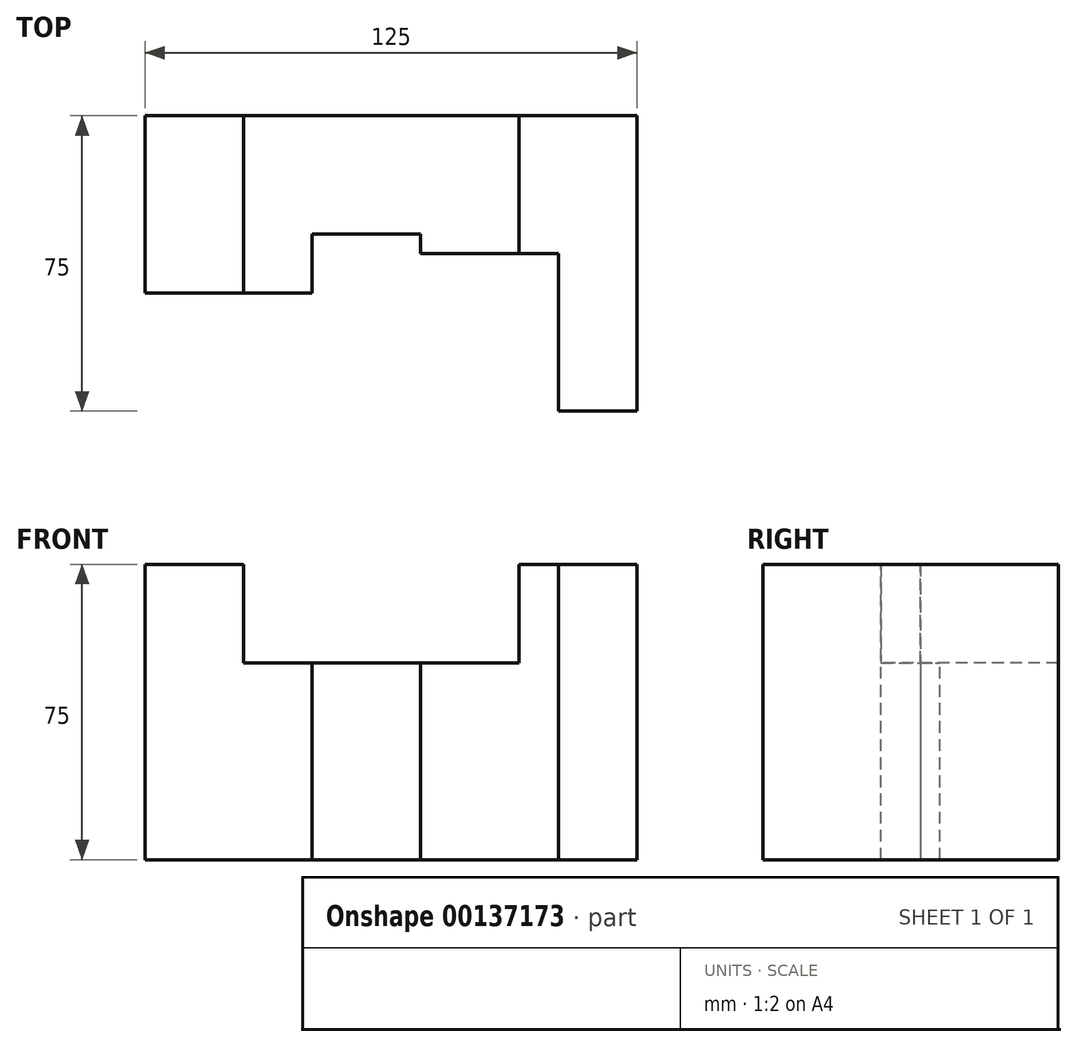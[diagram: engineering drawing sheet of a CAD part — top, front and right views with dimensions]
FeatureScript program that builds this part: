
annotation { "Feature Type Name" : "Feature", "Feature Type Description" : "" }
export const myFeature = defineFeature(function(context is Context, id is Id, definition is map)
    precondition{}
    {
        {
            var Q0;
            Q0=qCreatedBy(makeId("Front.planeOp"),FACE);
            var sketch = newSketch(context, id + "F0", { "sketchPlane" : qUnion([Q0])});
            skLineSegment(sketch, "E0.bottom", {"start": v(-62.95, 0) * mm, "end": v(62.05, 0) * mm});
            skLineSegment(sketch, "E0.top", {"start": v(-62.95, 75) * mm, "end": v(62.05, 75) * mm});
            skLineSegment(sketch, "E0.left", {"start": v(-62.95, 0) * mm, "end": v(-62.95, 75) * mm});
            skLineSegment(sketch, "E0.right", {"start": v(62.05, 0) * mm, "end": v(62.05, 75) * mm});
            skSolve(sketch);
        }
        {
            var Q0;
            Q0 = qSketchRegion(id + "F0", true);
            extrude(context, id + "F1", {"entities" : qUnion([Q0]), "endBound" : BoundingType.SYMMETRIC, "depth" : (15 * 5) * mm});
        }
        {
            var Q0;
            Q0=qCreatedBy(makeId("Top.planeOp"),FACE);
            var sketch = newSketch(context, id + "F2", { "sketchPlane" : qUnion([Q0])});
            skLineSegment(sketch, "E1.bottom", {"start": v(-62.95, -37.5) * mm, "end": v(42.05, -37.5) * mm});
            skLineSegment(sketch, "E1.left", {"start": v(-62.95, -37.5) * mm, "end": v(-62.95, -7.5) * mm});
            skLineSegment(sketch, "E1.right", {"start": v(42.05, -37.5) * mm, "end": v(42.05, -7.5) * mm});
            skLineSegment(sketch, "E2", {"start": v(-62.95, -7.5) * mm, "end": v(42.05, -7.5) * mm});
            skSolve(sketch);
        }
        {
            var Q0;
            Q0 = qSketchRegion(id + "F2", true);
            extrude(context, id + "F3", {"entities" : qUnion([Q0]), "operationType" : NewBodyOperationType.REMOVE, "endBound" : BoundingType.SYMMETRIC, "oppositeDirection" : true, "depth" : 150 * mm});
        }
        {
            var Q0;
            Q0=qCreatedBy(makeId("Top.planeOp"),FACE);
            var sketch = newSketch(context, id + "F4", { "sketchPlane" : qUnion([Q0])});
            skLineSegment(sketch, "E3.bottom", {"start": v(-37.95, 37.5) * mm, "end": v(32.05, 37.5) * mm});
            skLineSegment(sketch, "E3.top", {"start": v(-37.95, -7.5) * mm, "end": v(32.05, -7.5) * mm});
            skLineSegment(sketch, "E3.left", {"start": v(-37.95, 37.5) * mm, "end": v(-37.95, -7.5) * mm});
            skLineSegment(sketch, "E3.right", {"start": v(32.05, 37.5) * mm, "end": v(32.05, -7.5) * mm});
            skSolve(sketch);
        }
        {
            var Q0;
            Q0 = qSketchRegion(id + "F4", true);
            extrude(context, id + "F5", {"entities" : qUnion([Q0]), "operationType" : NewBodyOperationType.REMOVE, "depth" : 82.67 * mm, "hasSecondDirection" : true, "secondDirectionOppositeDirection" : false, "secondDirectionDepth" : 50 * mm});
        }
        {
            var Q0;
            Q0=qCreatedBy(makeId("Top.planeOp"),FACE);
            var sketch = newSketch(context, id + "F6", { "sketchPlane" : qUnion([Q0])});
            skLineSegment(sketch, "E4.bottom", {"start": v(-20.45, -7.5) * mm, "end": v(7.05, -7.5) * mm});
            skLineSegment(sketch, "E4.top", {"start": v(-20.45, 7.5) * mm, "end": v(7.05, 7.5) * mm});
            skLineSegment(sketch, "E4.left", {"start": v(-20.45, -7.5) * mm, "end": v(-20.45, 7.5) * mm});
            skLineSegment(sketch, "E4.right", {"start": v(7.05, -7.5) * mm, "end": v(7.05, 7.5) * mm});
            skSolve(sketch);
        }
        {
            var Q0;
            Q0 = qSketchRegion(id + "F6", true);
            extrude(context, id + "F7", {"entities" : qUnion([Q0]), "operationType" : NewBodyOperationType.REMOVE, "endBound" : BoundingType.SYMMETRIC, "oppositeDirection" : true, "depth" : 100 * mm});
        }
        {
            var Q0;
            Q0=qCreatedBy(makeId("Top.planeOp"),FACE);
            var sketch = newSketch(context, id + "F8", { "sketchPlane" : qUnion([Q0])});
            skLineSegment(sketch, "E5.bottom", {"start": v(7.05, -7.5) * mm, "end": v(42.05, -7.5) * mm});
            skLineSegment(sketch, "E5.top", {"start": v(7.05, 2.5) * mm, "end": v(42.05, 2.5) * mm});
            skLineSegment(sketch, "E5.left", {"start": v(7.05, -7.5) * mm, "end": v(7.05, 2.5) * mm});
            skLineSegment(sketch, "E5.right", {"start": v(42.05, -7.5) * mm, "end": v(42.05, 2.5) * mm});
            skSolve(sketch);
        }
        {
            var Q0;
            Q0 = qSketchRegion(id + "F8", true);
            extrude(context, id + "F9", {"entities" : qUnion([Q0]), "operationType" : NewBodyOperationType.REMOVE, "depth" : 79.67 * mm});
        }
    });
